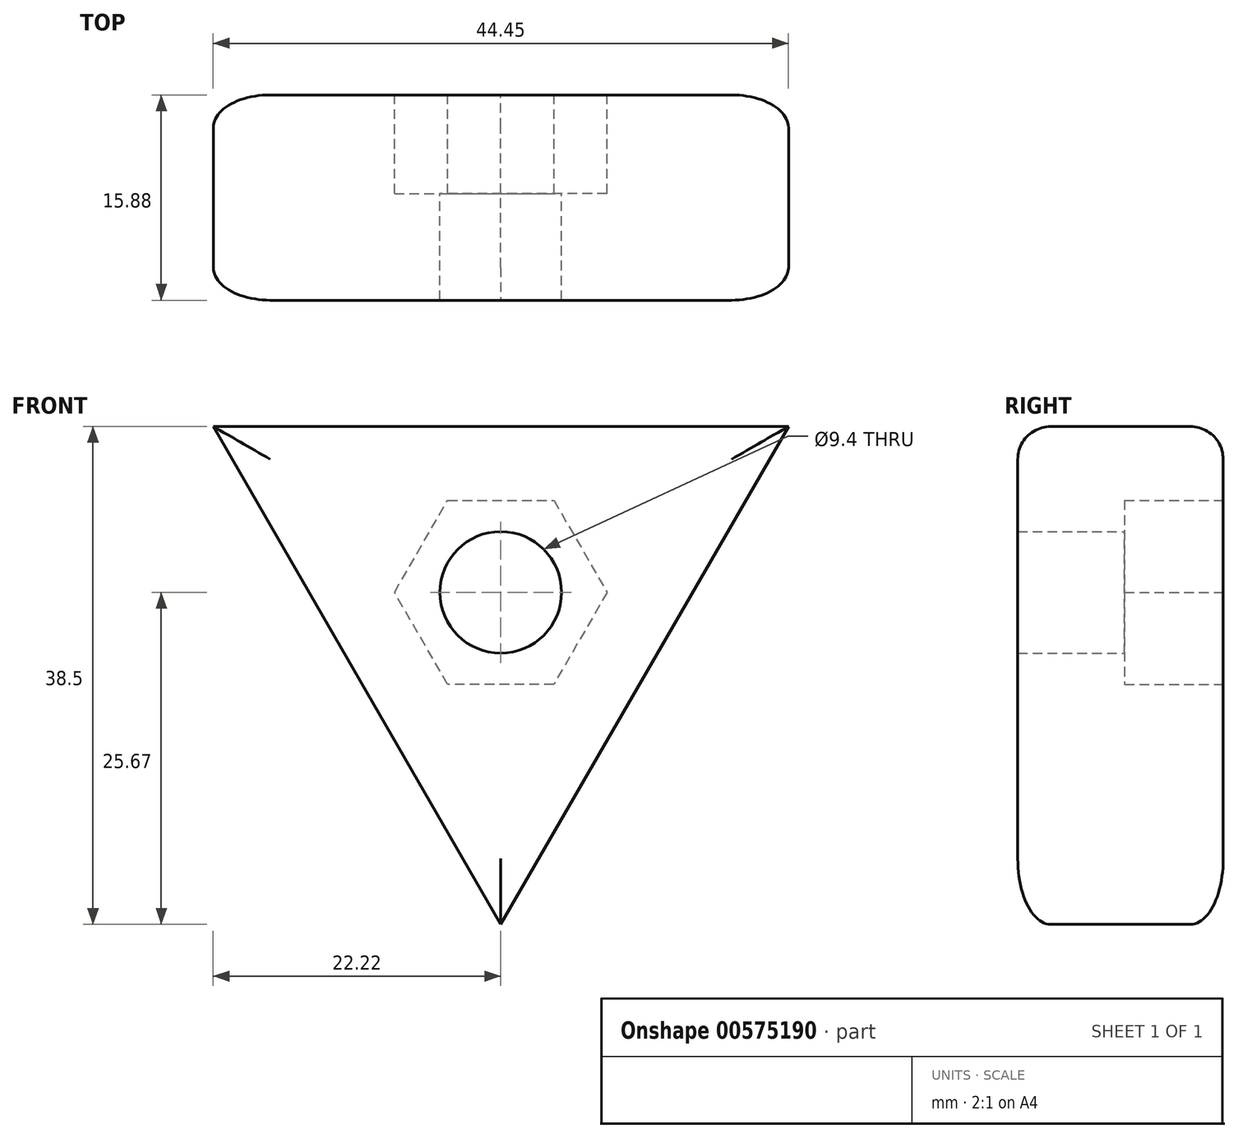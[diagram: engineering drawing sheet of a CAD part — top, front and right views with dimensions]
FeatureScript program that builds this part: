
annotation { "Feature Type Name" : "Feature", "Feature Type Description" : "" }
export const myFeature = defineFeature(function(context is Context, id is Id, definition is map)
    precondition{}
    {
        {
            var Q0;
            Q0=qCreatedBy(makeId("Front.planeOp"),FACE);
            var sketch = newSketch(context, id + "F0", { "sketchPlane" : qUnion([Q0])});
            skLineSegment(sketch, "E0", {"start": v(-22.22, 12.83) * mm, "end": v(22.23, 12.83) * mm});
            skLineSegment(sketch, "E1", {"start": v(22.23, 12.83) * mm, "end": v(0, -25.67) * mm});
            skLineSegment(sketch, "E2", {"start": v(-22.22, 12.83) * mm, "end": v(0, -25.67) * mm});
            skSolve(sketch);
        }
        {
            var Q0;
            Q0=qCreatedBy(makeId("Front.planeOp"),FACE);
            var sketch = newSketch(context, id + "F1", { "sketchPlane" : qUnion([Q0])});
            skLineSegment(sketch, "E3", {"start": v(0, 0) * mm, "end": v(6.16, -3.56) * mm});
            skCircle(sketch, "E4.cCircle", {"center": v(0, 0) * mm, "radius": 7.11 * mm, "construction": true});
            skLineSegment(sketch, "E4.0", {"start": v(8.21, 0) * mm, "end": v(4.1, -7.11) * mm});
            skLineSegment(sketch, "E4.1", {"start": v(4.1, -7.11) * mm, "end": v(-4.1, -7.11) * mm});
            skLineSegment(sketch, "E4.2", {"start": v(-4.1, -7.11) * mm, "end": v(-8.21, 0) * mm});
            skLineSegment(sketch, "E4.3", {"start": v(-8.21, 0) * mm, "end": v(-4.1, 7.11) * mm});
            skLineSegment(sketch, "E4.4", {"start": v(-4.1, 7.11) * mm, "end": v(4.1, 7.11) * mm});
            skLineSegment(sketch, "E4.5", {"start": v(4.1, 7.11) * mm, "end": v(8.21, 0) * mm});
            skPoint(sketch, "E4.0.midPoint", {"position": v(6.16, -3.56) * mm});
            skSolve(sketch);
        }
        {
            var Q0;
            Q0 = qSketchRegion(id + "F0", true);
            extrude(context, id + "F2", {"entities" : qUnion([Q0]), "depth" : 15.88 * mm, "offsetDistance" : 25.4 * mm});
        }
        {
            var Q0;
            Q0 = qSketchRegion(id + "F1", true);
            extrude(context, id + "F3", {"entities" : qUnion([Q0]), "operationType" : NewBodyOperationType.REMOVE, "depth" : 7.62 * mm, "offsetDistance" : 25.4 * mm});
        }
        {
            var Q0;
            Q0=qCreatedBy(makeId("Front.planeOp"),FACE);
            var sketch = newSketch(context, id + "F4", { "sketchPlane" : qUnion([Q0])});
            skCircle(sketch, "E5", {"center": v(0, 0) * mm, "radius": 4.7 * mm});
            skSolve(sketch);
        }
        {
            var Q0;
            Q0 = qSketchRegion(id + "F4", true);
            extrude(context, id + "F5", {"entities" : qUnion([Q0]), "operationType" : NewBodyOperationType.REMOVE, "depth" : 25.4 * mm, "offsetDistance" : 25.4 * mm});
        }
        {
            var Q0;
            Q0=makeQuery(id+"F2.opExtrude","CAP_EDGE",EDGE,{"disambiguationData":[OSD([sQuery(id+"F0.wireOp",EDGE,"E2")])],"isStart":true});
            var Q1;
            Q1=makeQuery(id+"F2.opExtrude","CAP_EDGE",EDGE,{"disambiguationData":[OSD([sQuery(id+"F0.wireOp",EDGE,"E0")])],"isStart":true});
            var Q2;
            Q2=makeQuery(id+"F2.opExtrude","CAP_EDGE",EDGE,{"disambiguationData":[OSD([sQuery(id+"F0.wireOp",EDGE,"E1")])],"isStart":true});
            var Q3;
            Q3=makeQuery(id+"F2.opExtrude","CAP_EDGE",EDGE,{"disambiguationData":[OSD([sQuery(id+"F0.wireOp",EDGE,"E0")])],"isStart":false});
            var Q4;
            Q4=makeQuery(id+"F2.opExtrude","CAP_EDGE",EDGE,{"disambiguationData":[OSD([sQuery(id+"F0.wireOp",EDGE,"E2")])],"isStart":false});
            var Q5;
            Q5=makeQuery(id+"F2.opExtrude","CAP_EDGE",EDGE,{"disambiguationData":[OSD([sQuery(id+"F0.wireOp",EDGE,"E1")])],"isStart":false});
            fillet(context, id + "F6", {"entities" : qUnion([Q0, Q1, Q2, Q3, Q4, Q5]), "radius" : 2.54 * mm, "tangentPropagation" : true, "allowEdgeOverflow" : false});
        }
    });
